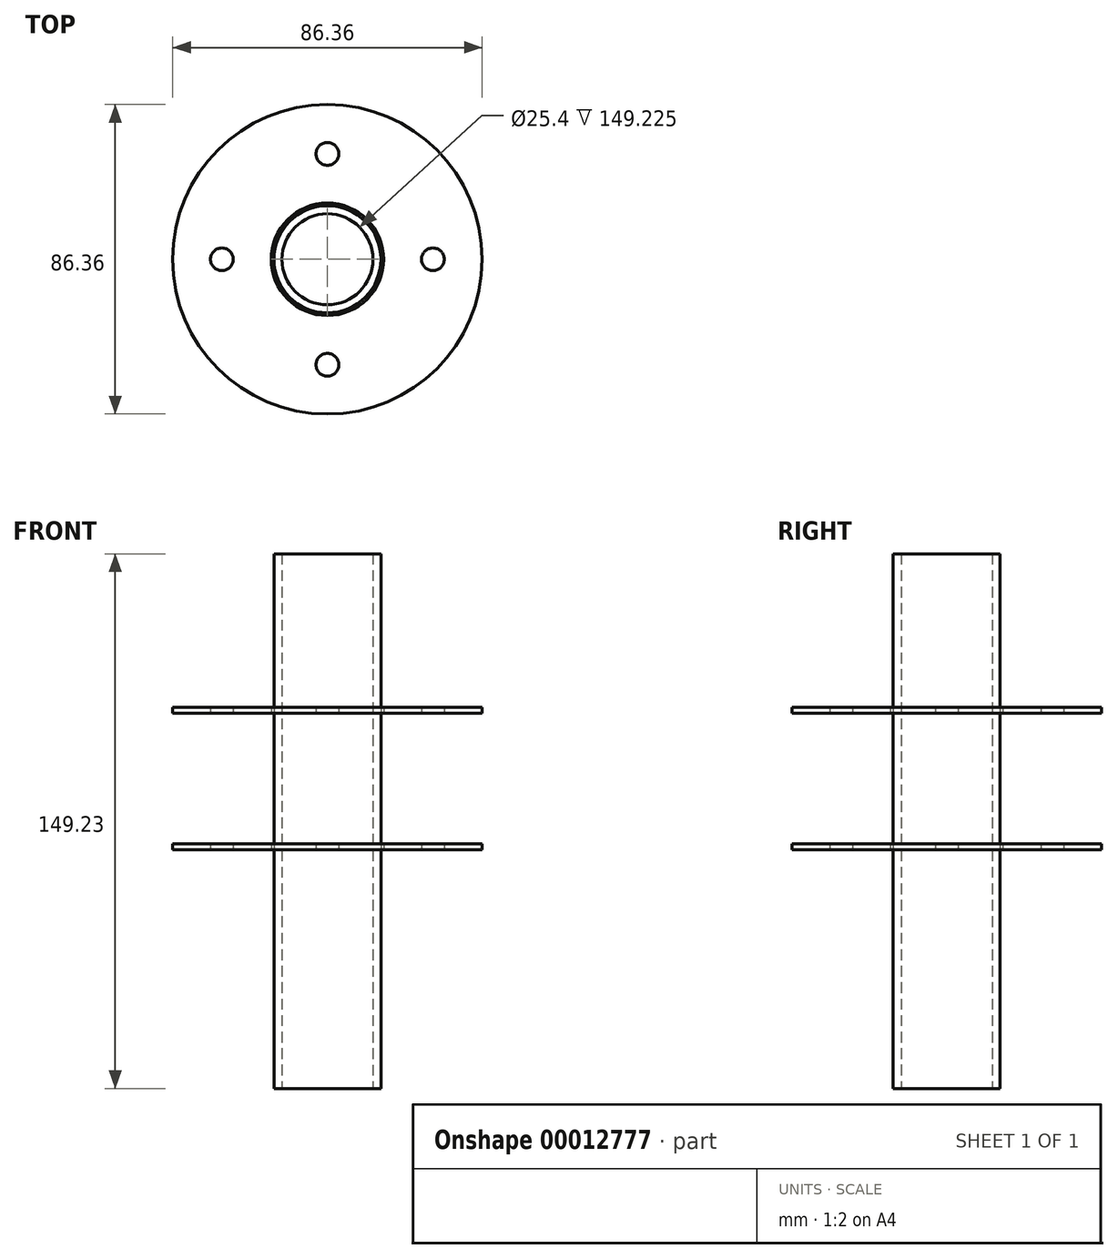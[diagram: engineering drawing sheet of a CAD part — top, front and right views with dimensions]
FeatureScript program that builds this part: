
annotation { "Feature Type Name" : "Feature", "Feature Type Description" : "" }
export const myFeature = defineFeature(function(context is Context, id is Id, definition is map)
    precondition{}
    {
        {
            var Q0;
            Q0=qCreatedBy(makeId("Top.planeOp"),FACE);
            var sketch = newSketch(context, id + "F0", { "sketchPlane" : qUnion([Q0])});
            skCircle(sketch, "E0", {"center": v(0, 0) * mm, "radius": 12.7 * mm});
            skCircle(sketch, "E1.0", {"center": v(0, 0) * mm, "radius": 14.94 * mm});
            skSolve(sketch);
        }
        {
            var Q0;
            Q0=makeQuery(id+"F0.imprint","IMPRINT",FACE,{"disambiguationData":[TD([[makeQuery(id+"F0.imprint","IMPRINT",EDGE,{"derivedFrom":sQuery(id+"F0.wireOp",EDGE,"E0")}),-1.0]])]});
            extrude(context, id + "F1", {"entities" : qUnion([Q0]), "depth" : 149.22 * mm});
        }
        {
            var Q0;
            Q0=qCreatedBy(makeId("Top.planeOp"),FACE);
            var sketch = newSketch(context, id + "F2", { "sketchPlane" : qUnion([Q0])});
            skCircle(sketch, "E2", {"center": v(0, 0) * mm, "radius": 43.18 * mm});
            skCircle(sketch, "E3.0", {"center": v(0, 0) * mm, "radius": 15.7 * mm});
            skCircle(sketch, "E4", {"center": v(0, 29.44) * mm, "radius": 3.18 * mm});
            skCircle(sketch, "E5.1.0", {"center": v(-29.44, 0) * mm, "radius": 3.18 * mm});
            skCircle(sketch, "E5.2.0", {"center": v(0, -29.44) * mm, "radius": 3.18 * mm});
            skCircle(sketch, "E5.3.0", {"center": v(29.44, 0) * mm, "radius": 3.18 * mm});
            skSolve(sketch);
        }
        {
            var Q0;
            Q0=makeQuery(id+"F2.imprint","IMPRINT",FACE,{"disambiguationData":[TD([[makeQuery(id+"F2.imprint","IMPRINT",EDGE,{"derivedFrom":sQuery(id+"F2.wireOp",EDGE,"E2")}),1.0]])]});
            extrude(context, id + "F3", {"entities" : qUnion([Q0]), "depth" : 1.59 * mm});
        }
        {
            var Q0;
            Q0=makeQuery(id+"F3.opExtrude","SWEPT_BODY",BODY,{"disambiguationData":[OSD([sQuery(id+"F2.wireOp",EDGE,"E2"),sQuery(id+"F2.wireOp",EDGE,"E3.0"),sQuery(id+"F2.wireOp",EDGE,"E4"),sQuery(id+"F2.wireOp",EDGE,"E5.1.0"),sQuery(id+"F2.wireOp",EDGE,"E5.2.0"),sQuery(id+"F2.wireOp",EDGE,"E5.3.0")])]});
            transform(context, id + "F4", {"entities" : qUnion([Q0]), "transformType" : TransformType.TRANSLATION_3D, "dx" : 0 * mm, "dy" : 0 * mm, "dz" : 66.67 * mm, "makeCopy" : false});
        }
        {
            var Q0;
            Q0=makeQuery(id+"F3.opExtrude","SWEPT_BODY",BODY,{"disambiguationData":[OSD([sQuery(id+"F2.wireOp",EDGE,"E2"),sQuery(id+"F2.wireOp",EDGE,"E3.0"),sQuery(id+"F2.wireOp",EDGE,"E4"),sQuery(id+"F2.wireOp",EDGE,"E5.1.0"),sQuery(id+"F2.wireOp",EDGE,"E5.2.0"),sQuery(id+"F2.wireOp",EDGE,"E5.3.0")])]});
            transform(context, id + "F5", {"entities" : qUnion([Q0]), "transformType" : TransformType.TRANSLATION_3D, "dx" : 0 * mm, "dy" : 0 * mm, "dz" : 38.1 * mm, "makeCopy" : true});
        }
    });
